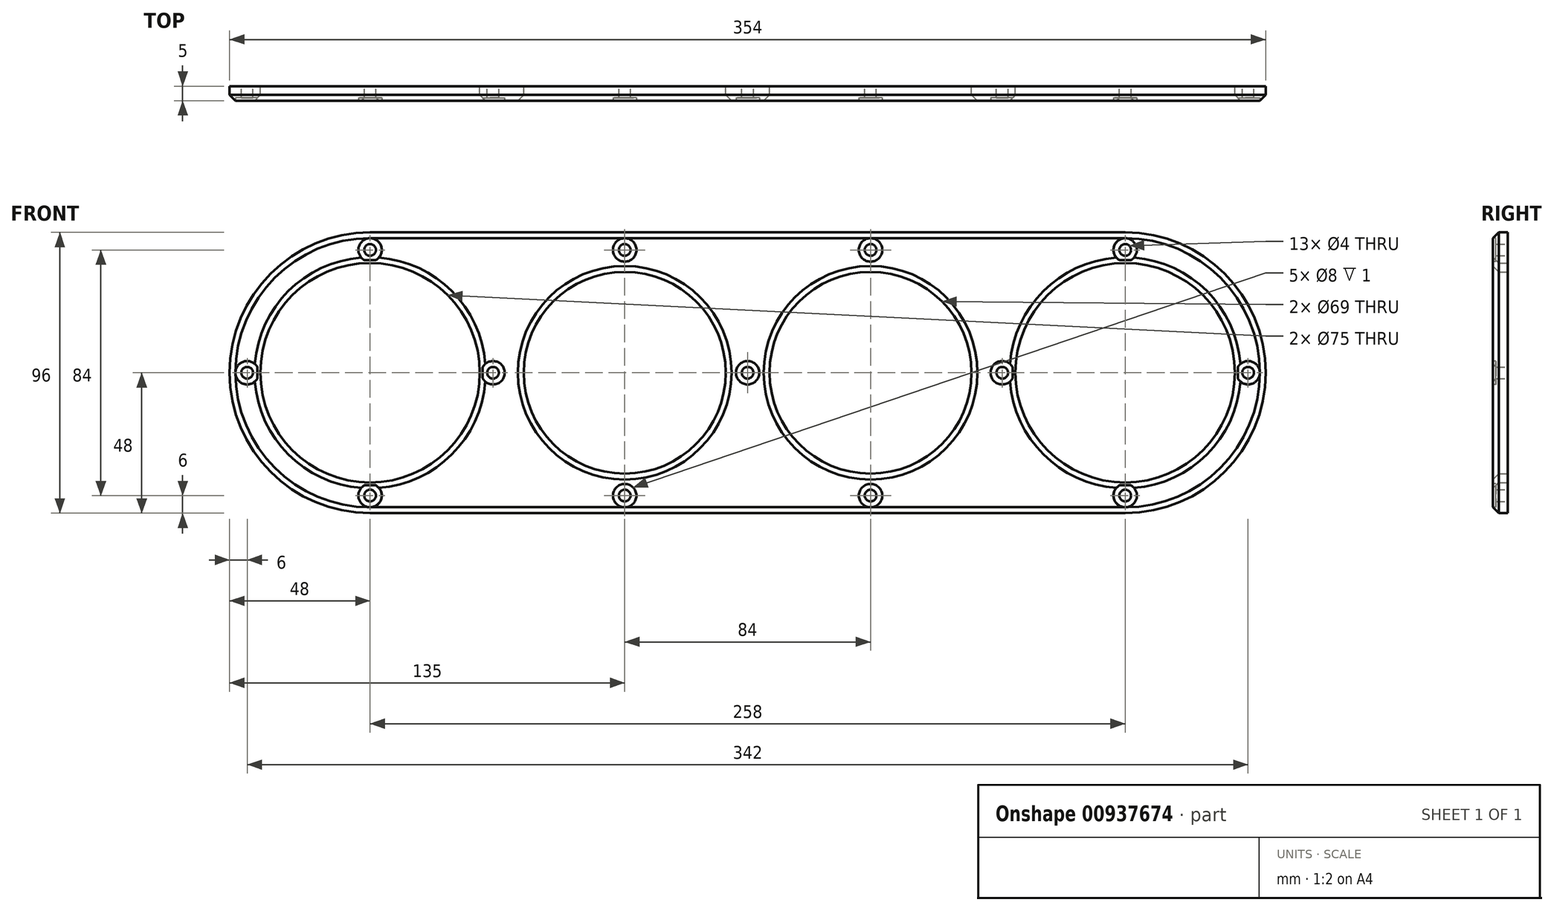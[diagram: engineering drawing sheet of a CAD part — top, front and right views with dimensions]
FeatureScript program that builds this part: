
annotation { "Feature Type Name" : "Feature", "Feature Type Description" : "" }
export const myFeature = defineFeature(function(context is Context, id is Id, definition is map)
    precondition{}
    {
        {
            var Q0;
            Q0=qCreatedBy(makeId("Front.planeOp"),FACE);
            var sketch = newSketch(context, id + "F0", { "sketchPlane" : qUnion([Q0])});
            skCircle(sketch, "E0", {"center": v(42, 0) * mm, "radius": 34.5 * mm});
            skCircle(sketch, "E1", {"center": v(129, 0) * mm, "radius": 37.5 * mm});
            skLineSegment(sketch, "E2", {"start": v(0, -113.77) * mm, "end": v(0, 113.17) * mm, "construction": true});
            skArc(sketch, "E3", {"start": v(129, 48) * mm, "mid": v(177, 0) * mm, "end": v(129, -48) * mm});
            skLineSegment(sketch, "E4", {"start": v(129, -48) * mm, "end": v(0, -48) * mm});
            skLineSegment(sketch, "E5", {"start": v(129, 48) * mm, "end": v(0, 48) * mm});
            skLineSegment(sketch, "E6.MirrorCS", {"start": v(-129, -48) * mm, "end": v(0, -48) * mm});
            skLineSegment(sketch, "E7.MirrorCS", {"start": v(-129, 48) * mm, "end": v(0, 48) * mm});
            skArc(sketch, "E8.MirrorCS", {"start": v(-129, 48) * mm, "mid": v(-177, 0) * mm, "end": v(-129, -48) * mm});
            skCircle(sketch, "E9.MirrorC", {"center": v(-129, 0) * mm, "radius": 37.5 * mm});
            skCircle(sketch, "E10.MirrorC", {"center": v(-42, 0) * mm, "radius": 34.5 * mm});
            skCircle(sketch, "E11", {"center": v(129, 42) * mm, "radius": 2 * mm});
            skCircle(sketch, "E12.1.0", {"center": v(87, 0) * mm, "radius": 2 * mm});
            skCircle(sketch, "E12.2.0", {"center": v(129, -42) * mm, "radius": 2 * mm});
            skCircle(sketch, "E12.3.0", {"center": v(171, 0) * mm, "radius": 2 * mm});
            skCircle(sketch, "E13.MirrorC", {"center": v(-171, 0) * mm, "radius": 2 * mm});
            skCircle(sketch, "E14.MirrorC", {"center": v(-129, 42) * mm, "radius": 2 * mm});
            skCircle(sketch, "E15.MirrorC", {"center": v(-129, -42) * mm, "radius": 2 * mm});
            skCircle(sketch, "E16.MirrorC", {"center": v(-87, 0) * mm, "radius": 2 * mm});
            skCircle(sketch, "E17", {"center": v(42, 42) * mm, "radius": 2 * mm});
            skCircle(sketch, "E18.1.0", {"center": v(42, -42) * mm, "radius": 2 * mm});
            skCircle(sketch, "E19.MirrorC", {"center": v(-42, 42) * mm, "radius": 2 * mm});
            skCircle(sketch, "E20.MirrorC", {"center": v(-42, -42) * mm, "radius": 2 * mm});
            skCircle(sketch, "E21", {"center": v(0, 0) * mm, "radius": 2 * mm});
            skSolve(sketch);
        }
        {
            var Q0;
            Q0=qSketchRegion(id+"F0",true);
            extrude(context, id + "F1", {"entities" : qUnion([Q0]), "depth" : 5 * mm, "offsetDistance" : 25 * mm});
        }
        {
            var Q0;
            Q0=makeQuery(id+"F1.opExtrude","CAP_EDGE",EDGE,{"disambiguationData":[OSD([sQuery(id+"F0.wireOp",EDGE,"E0")])],"isStart":false});
            var Q1;
            Q1=makeQuery(id+"F1.opExtrude","CAP_EDGE",EDGE,{"disambiguationData":[OSD([sQuery(id+"F0.wireOp",EDGE,"E10.MirrorC")])],"isStart":false});
            chamfer(context, id + "F2", {"entities" : qUnion([Q0, Q1]), "width" : 2 * mm, "tangentPropagation" : true});
        }
        {
            var Q0;
            Q0=makeQuery(id+"F1.opExtrude","CAP_EDGE",EDGE,{"disambiguationData":[OSD([sQuery(id+"F0.wireOp",EDGE,"E1")])],"isStart":false});
            var Q1;
            Q1=makeQuery(id+"F1.opExtrude","CAP_EDGE",EDGE,{"disambiguationData":[OSD([sQuery(id+"F0.wireOp",EDGE,"E9.MirrorC")])],"isStart":false});
            chamfer(context, id + "F3", {"entities" : qUnion([Q0, Q1]), "width" : 2 * mm, "tangentPropagation" : true});
        }
        {
            var Q0;
            Q0=makeQuery(id+"F1.opExtrude","CAP_FACE",FACE,{"disambiguationData":[OSD([sQuery(id+"F0.wireOp",EDGE,"E0"),sQuery(id+"F0.wireOp",EDGE,"E1"),sQuery(id+"F0.wireOp",EDGE,"E3"),sQuery(id+"F0.wireOp",EDGE,"E4"),sQuery(id+"F0.wireOp",EDGE,"E5"),sQuery(id+"F0.wireOp",EDGE,"E6.MirrorCS"),sQuery(id+"F0.wireOp",EDGE,"E7.MirrorCS"),sQuery(id+"F0.wireOp",EDGE,"E8.MirrorCS"),sQuery(id+"F0.wireOp",EDGE,"E9.MirrorC"),sQuery(id+"F0.wireOp",EDGE,"E10.MirrorC"),sQuery(id+"F0.wireOp",EDGE,"E11"),sQuery(id+"F0.wireOp",EDGE,"E12.1.0"),sQuery(id+"F0.wireOp",EDGE,"E12.2.0"),sQuery(id+"F0.wireOp",EDGE,"E12.3.0"),sQuery(id+"F0.wireOp",EDGE,"E13.MirrorC"),sQuery(id+"F0.wireOp",EDGE,"E14.MirrorC"),sQuery(id+"F0.wireOp",EDGE,"E15.MirrorC"),sQuery(id+"F0.wireOp",EDGE,"E16.MirrorC"),sQuery(id+"F0.wireOp",EDGE,"E17"),sQuery(id+"F0.wireOp",EDGE,"E18.1.0"),sQuery(id+"F0.wireOp",EDGE,"E19.MirrorC"),sQuery(id+"F0.wireOp",EDGE,"E20.MirrorC"),sQuery(id+"F0.wireOp",EDGE,"E21")])],"isStart":false});
            var sketch = newSketch(context, id + "F4", { "sketchPlane" : qUnion([Q0])});
            skCircle(sketch, "E22", {"center": v(0, 0) * mm, "radius": 4 * mm});
            skCircle(sketch, "E23", {"center": v(42, 42) * mm, "radius": 4 * mm});
            skCircle(sketch, "E24", {"center": v(42, -42) * mm, "radius": 4 * mm});
            skCircle(sketch, "E25", {"center": v(129, 42) * mm, "radius": 4 * mm});
            skCircle(sketch, "E26.1.0", {"center": v(87, 0) * mm, "radius": 4 * mm});
            skCircle(sketch, "E26.2.0", {"center": v(129, -42) * mm, "radius": 4 * mm});
            skCircle(sketch, "E26.3.0", {"center": v(171, 0) * mm, "radius": 4 * mm});
            skPoint(sketch, "E26.center", {"position": v(129, 0) * mm});
            skLineSegment(sketch, "E27", {"start": v(0, 65.68) * mm, "end": v(0, -63.83) * mm, "construction": true});
            skPoint(sketch, "E27.endSnap0", {"position": v(0, -48) * mm});
            skCircle(sketch, "E28.MirrorC", {"center": v(-42, 42) * mm, "radius": 4 * mm});
            skCircle(sketch, "E29.MirrorC", {"center": v(-42, -42) * mm, "radius": 4 * mm});
            skCircle(sketch, "E30.MirrorC", {"center": v(-87, 0) * mm, "radius": 4 * mm});
            skCircle(sketch, "E31.MirrorC", {"center": v(-129, -42) * mm, "radius": 4 * mm});
            skCircle(sketch, "E32.MirrorC", {"center": v(-129, 42) * mm, "radius": 4 * mm});
            skCircle(sketch, "E33.MirrorC", {"center": v(-171, 0) * mm, "radius": 4 * mm});
            skSolve(sketch);
        }
        {
            var Q0;
            Q0=qSketchRegion(id+"F4",true);
            extrude(context, id + "F5", {"entities" : qUnion([Q0]), "operationType" : NewBodyOperationType.REMOVE, "oppositeDirection" : true, "depth" : 1 * mm, "offsetDistance" : 25 * mm});
        }
        {
            var Q0;
            Q0=makeQuery(id+"F1.opExtrude","CAP_EDGE",EDGE,{"disambiguationData":[OSD([sQuery(id+"F0.wireOp",EDGE,"E8.MirrorCS")])],"isStart":false});
            var Q1;
            Q1=makeQuery(id+"F1.opExtrude","CAP_EDGE",EDGE,{"disambiguationData":[OSD([sQuery(id+"F0.wireOp",EDGE,"E5"),sQuery(id+"F0.wireOp",EDGE,"E7.MirrorCS")])],"isStart":false});
            var Q2;
            Q2=makeQuery(id+"F1.opExtrude","CAP_EDGE",EDGE,{"disambiguationData":[OSD([sQuery(id+"F0.wireOp",EDGE,"E4"),sQuery(id+"F0.wireOp",EDGE,"E6.MirrorCS")])],"isStart":false});
            var Q3;
            Q3=makeQuery(id+"F1.opExtrude","CAP_EDGE",EDGE,{"disambiguationData":[OSD([sQuery(id+"F0.wireOp",EDGE,"E3")])],"isStart":false});
            chamfer(context, id + "F6", {"entities" : qUnion([Q0, Q1, Q2, Q3]), "width" : 2 * mm, "tangentPropagation" : true});
        }
    });
